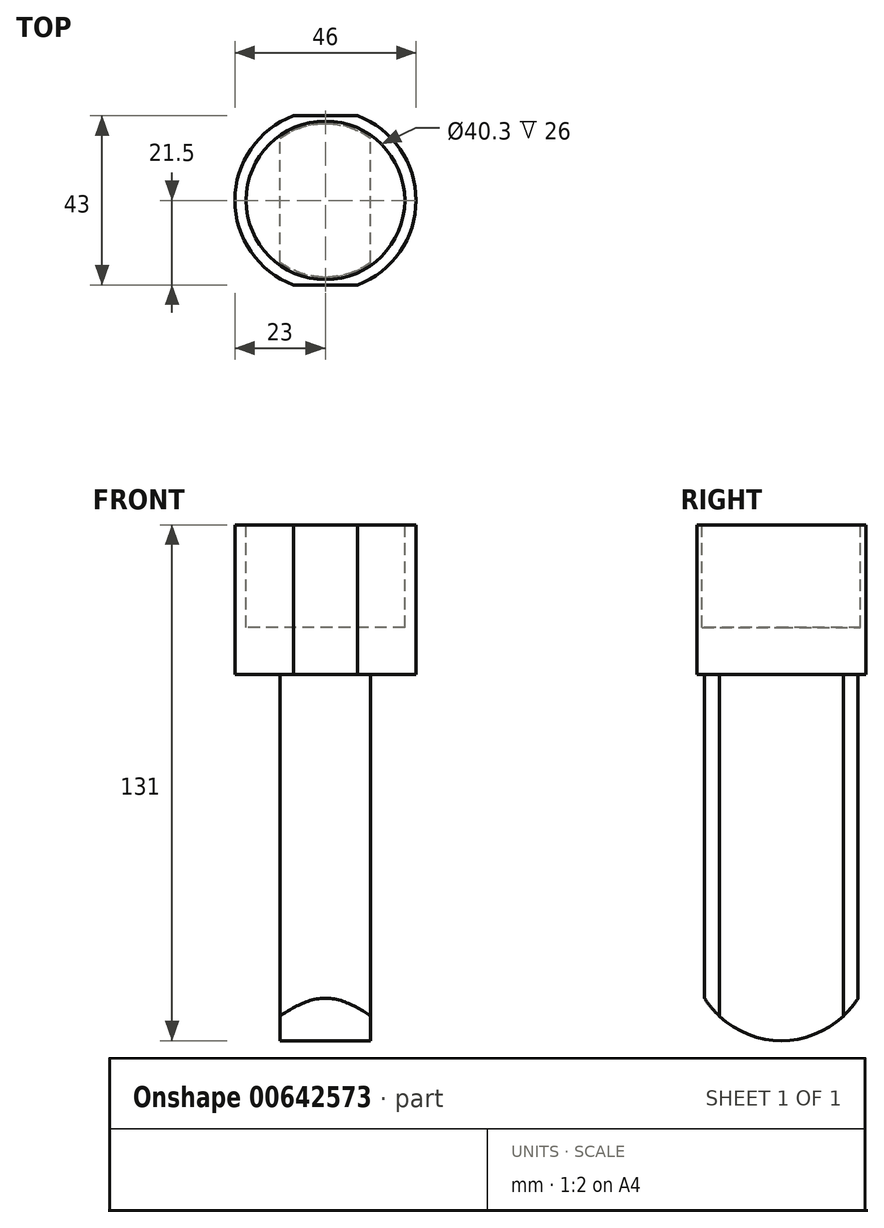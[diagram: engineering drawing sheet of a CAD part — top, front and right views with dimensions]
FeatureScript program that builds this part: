
annotation { "Feature Type Name" : "Feature", "Feature Type Description" : "" }
export const myFeature = defineFeature(function(context is Context, id is Id, definition is map)
    precondition{}
    {
        {
            var Q0;
            Q0=qCreatedBy(makeId("Top.planeOp"),FACE);
            var sketch = newSketch(context, id + "F0", { "sketchPlane" : qUnion([Q0])});
            skArc(sketch, "E0", {"start": v(-8.17, 21.5) * mm, "mid": v(-23, 0) * mm, "end": v(-8.17, -21.5) * mm});
            skLineSegment(sketch, "E1", {"start": v(-8.17, 21.5) * mm, "end": v(8.17, 21.5) * mm});
            skLineSegment(sketch, "E2.MirrorCS", {"start": v(-8.17, -21.5) * mm, "end": v(8.17, -21.5) * mm});
            skArc(sketch, "E3.trimOffspring", {"start": v(8.17, -21.5) * mm, "mid": v(23, 0) * mm, "end": v(8.17, 21.5) * mm});
            skSolve(sketch);
        }
        {
            var Q0;
            Q0 = qSketchRegion(id + "F0", true);
            var Q1;
            Q1=makeQuery(id+"F0.imprint","IMPRINT",FACE,{"disambiguationData":[TD([[makeQuery(id+"F0.imprint","IMPRINT",EDGE,{"derivedFrom":sQuery(id+"F0.wireOp",EDGE,"E0")}),1.0]])]});
            extrude(context, id + "F1", {"entities" : qUnion([Q0, Q1]), "depth" : 38 * mm, "offsetDistance" : 25 * mm});
        }
        {
            var Q0;
            Q0=makeQuery(id+"F1.opExtrude","CAP_FACE",FACE,{"disambiguationData":[OSD([sQuery(id+"F0.wireOp",EDGE,"E0"),sQuery(id+"F0.wireOp",EDGE,"E1"),sQuery(id+"F0.wireOp",EDGE,"E2.MirrorCS"),sQuery(id+"F0.wireOp",EDGE,"E3.trimOffspring")])],"isStart":false});
            var sketch = newSketch(context, id + "F2", { "sketchPlane" : qUnion([Q0])});
            skCircle(sketch, "E4", {"center": v(0, 0) * mm, "radius": 20.15 * mm});
            skSolve(sketch);
        }
        {
            var Q0;
            Q0=makeQuery(id+"F2.imprint","IMPRINT",FACE,{"disambiguationData":[TD([[makeQuery(id+"F2.imprint","IMPRINT",EDGE,{"derivedFrom":sQuery(id+"F2.wireOp",EDGE,"E4")}),1.0]])]});
            extrude(context, id + "F3", {"entities" : qUnion([Q0]), "operationType" : NewBodyOperationType.REMOVE, "oppositeDirection" : true, "depth" : 26 * mm, "offsetDistance" : 25 * mm});
        }
        {
            var Q0;
            Q0=makeQuery(id+"F1.opExtrude","CAP_FACE",FACE,{"disambiguationData":[OSD([sQuery(id+"F0.wireOp",EDGE,"E0"),sQuery(id+"F0.wireOp",EDGE,"E1"),sQuery(id+"F0.wireOp",EDGE,"E2.MirrorCS"),sQuery(id+"F0.wireOp",EDGE,"E3.trimOffspring")])],"isStart":true});
            var sketch = newSketch(context, id + "F4", { "sketchPlane" : qUnion([Q0])});
            skArc(sketch, "E5", {"start": v(-11.5, -15.75) * mm, "mid": v(0, -19.5) * mm, "end": v(11.5, -15.75) * mm});
            skLineSegment(sketch, "E6", {"start": v(-11.5, 15.75) * mm, "end": v(-11.5, -15.75) * mm});
            skLineSegment(sketch, "E7.MirrorCS", {"start": v(11.5, 15.75) * mm, "end": v(11.5, -15.75) * mm});
            skArc(sketch, "E8.trimOffspring", {"start": v(11.5, 15.75) * mm, "mid": v(0, 19.5) * mm, "end": v(-11.5, 15.75) * mm});
            skSolve(sketch);
        }
        {
            var Q0;
            Q0=makeQuery(id+"F4.imprint","IMPRINT",FACE,{"disambiguationData":[TD([[makeQuery(id+"F4.imprint","IMPRINT",EDGE,{"derivedFrom":sQuery(id+"F4.wireOp",EDGE,"E5")}),1.0]])]});
            extrude(context, id + "F5", {"entities" : qUnion([Q0]), "operationType" : NewBodyOperationType.ADD, "depth" : 93 * mm, "offsetDistance" : 25 * mm});
        }
        {
            var Q0;
            Q0=makeQuery(id+"F5.opExtrude","SWEPT_FACE",FACE,{"disambiguationData":[OSD([sQuery(id+"F4.wireOp",EDGE,"E7.MirrorCS")])]});
            var sketch = newSketch(context, id + "F6", { "sketchPlane" : qUnion([Q0])});
            skArc(sketch, "E9", {"start": v(-19.49, -82.22) * mm, "mid": v(0, -93) * mm, "end": v(19.48, -82.23) * mm});
            skLineSegment(sketch, "E10", {"start": v(-19.49, -82.22) * mm, "end": v(-28.91, -105.74) * mm});
            skLineSegment(sketch, "E11", {"start": v(-28.91, -105.74) * mm, "end": v(31.31, -98.2) * mm});
            skLineSegment(sketch, "E12", {"start": v(31.31, -98.2) * mm, "end": v(19.48, -82.23) * mm});
            skSolve(sketch);
        }
        {
            var Q0;
            {var subQ0=sQuery(id+"F6.wireOp",EDGE,"E10");Q0=makeQuery(id+"F6.imprint","IMPRINT",FACE,{"disambiguationData":[TD([[makeQuery(id+"F6.imprint","IMPRINT",EDGE,{"derivedFrom":subQ0}),1.0]])]});}
            var Q1;
            {var subQ0=sQuery(id+"F6.wireOp",EDGE,"E9");var subQ1=sQuery(id+"F4.wireOp",EDGE,"E7.MirrorCS");var subQ4=makeQuery(id+"F5.opExtrude","CAP_EDGE",EDGE,{"disambiguationData":[OSD([subQ1])],"isStart":false});var subQ5=makeQuery(id+"F6.imprint","INTERSECT",VERTEX,{"derivedFrom":[subQ4,subQ0]});Q1=makeQuery(id+"F6.imprint","IMPRINT",FACE,{"disambiguationData":[TD([[makeQuery(id+"F6.imprint","IMPRINT",EDGE,{"disambiguationData":[TD([[subQ5,1.0]])],"derivedFrom":subQ0}),-1.0]])]});}
            var Q2;
            {var subQ0=sQuery(id+"F6.wireOp",EDGE,"E9");var subQ1=sQuery(id+"F4.wireOp",EDGE,"E7.MirrorCS");var subQ4=makeQuery(id+"F5.opExtrude","CAP_EDGE",EDGE,{"disambiguationData":[OSD([subQ1])],"isStart":false});var subQ5=makeQuery(id+"F6.imprint","INTERSECT",VERTEX,{"derivedFrom":[subQ4,subQ0]});Q2=makeQuery(id+"F6.imprint","IMPRINT",FACE,{"disambiguationData":[TD([[makeQuery(id+"F6.imprint","IMPRINT",EDGE,{"disambiguationData":[TD([[subQ5,-1.0]])],"derivedFrom":subQ0}),-1.0]])]});}
            extrude(context, id + "F7", {"entities" : qUnion([Q0, Q1, Q2]), "operationType" : NewBodyOperationType.REMOVE, "oppositeDirection" : true, "depth" : 25 * mm, "offsetDistance" : 25 * mm});
        }
    });
